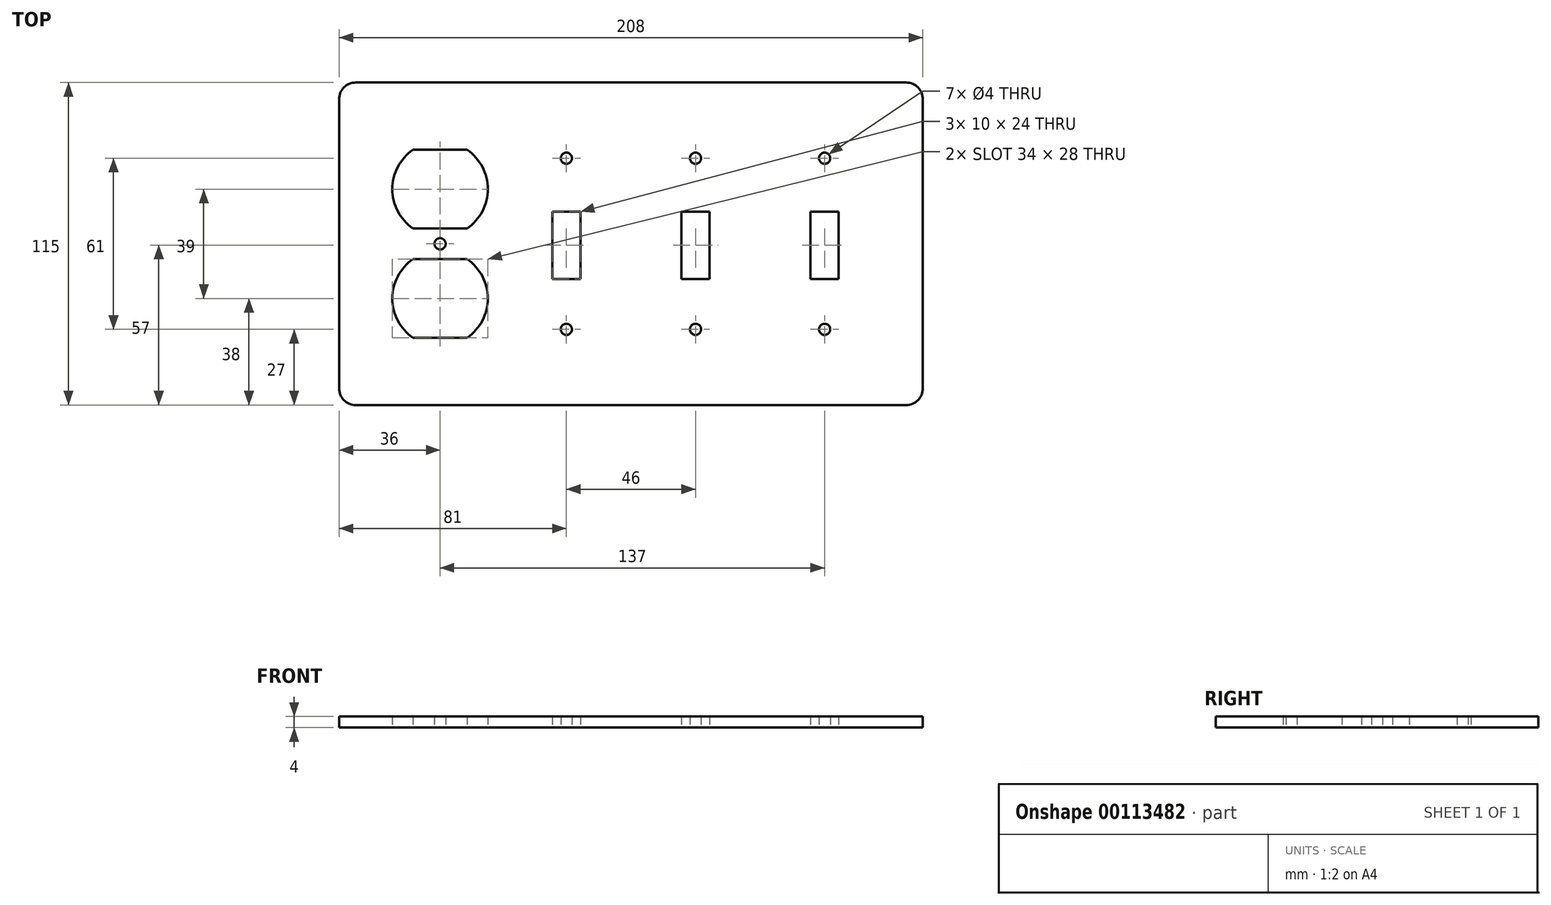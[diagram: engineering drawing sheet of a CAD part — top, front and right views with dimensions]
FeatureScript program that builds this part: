
annotation { "Feature Type Name" : "Feature", "Feature Type Description" : "" }
export const myFeature = defineFeature(function(context is Context, id is Id, definition is map)
    precondition{}
    {
        {
            var Q0;
            Q0=qCreatedBy(makeId("Top.planeOp"),FACE);
            var sketch = newSketch(context, id + "F0", { "sketchPlane" : qUnion([Q0])});
            skLineSegment(sketch, "E0.bottom", {"start": v(0, 0) * mm, "end": v(208, 0) * mm});
            skLineSegment(sketch, "E0.top", {"start": v(0, 115) * mm, "end": v(208, 115) * mm});
            skLineSegment(sketch, "E0.left", {"start": v(0, 0) * mm, "end": v(0, 115) * mm});
            skLineSegment(sketch, "E0.right", {"start": v(208, 0) * mm, "end": v(208, 115) * mm});
            skLineSegment(sketch, "E1.bottom", {"start": v(168, 69) * mm, "end": v(178, 69) * mm});
            skLineSegment(sketch, "E1.top", {"start": v(168, 45) * mm, "end": v(178, 45) * mm});
            skLineSegment(sketch, "E1.left", {"start": v(168, 69) * mm, "end": v(168, 45) * mm});
            skLineSegment(sketch, "E1.right", {"start": v(178, 69) * mm, "end": v(178, 45) * mm});
            skCircle(sketch, "E2", {"center": v(173, 88) * mm, "radius": 2 * mm});
            skCircle(sketch, "E3", {"center": v(173, 27) * mm, "radius": 2 * mm});
            skLineSegment(sketch, "E4.1.0.0", {"start": v(122, 69) * mm, "end": v(122, 45) * mm});
            skLineSegment(sketch, "E4.1.0.1", {"start": v(122, 45) * mm, "end": v(132, 45) * mm});
            skLineSegment(sketch, "E4.1.0.2", {"start": v(122, 69) * mm, "end": v(132, 69) * mm});
            skLineSegment(sketch, "E4.1.0.3", {"start": v(132, 69) * mm, "end": v(132, 45) * mm});
            skCircle(sketch, "E4.1.0.4", {"center": v(127, 88) * mm, "radius": 2 * mm});
            skCircle(sketch, "E4.1.0.5", {"center": v(127, 27) * mm, "radius": 2 * mm});
            skLineSegment(sketch, "E4.2.0.0", {"start": v(76, 69) * mm, "end": v(76, 45) * mm});
            skLineSegment(sketch, "E4.2.0.1", {"start": v(76, 45) * mm, "end": v(86, 45) * mm});
            skLineSegment(sketch, "E4.2.0.2", {"start": v(76, 69) * mm, "end": v(86, 69) * mm});
            skLineSegment(sketch, "E4.2.0.3", {"start": v(86, 69) * mm, "end": v(86, 45) * mm});
            skCircle(sketch, "E4.2.0.4", {"center": v(81, 88) * mm, "radius": 2 * mm});
            skCircle(sketch, "E4.2.0.5", {"center": v(81, 27) * mm, "radius": 2 * mm});
            skLineSegment(sketch, "E4.direction1", {"start": v(173, 27) * mm, "end": v(127, 27) * mm, "construction": true});
            skSolve(sketch);
        }
        {
            var Q0;
            Q0=qSketchRegion(id+"F0",true);
            extrude(context, id + "F1", {"entities" : qUnion([Q0]), "depth" : 4 * mm});
        }
        {
            var Q0;
            Q0=makeQuery(id+"F1.opExtrude","SWEPT_EDGE",EDGE,{"disambiguationData":[OSD([sQuery(id+"F0.wireOp",EDGE,"E0.top"),sQuery(id+"F0.wireOp",EDGE,"E0.left")])]});
            var Q1;
            Q1=makeQuery(id+"F1.opExtrude","SWEPT_EDGE",EDGE,{"disambiguationData":[OSD([sQuery(id+"F0.wireOp",EDGE,"E0.top"),sQuery(id+"F0.wireOp",EDGE,"E0.right")])]});
            var Q2;
            Q2=makeQuery(id+"F1.opExtrude","SWEPT_EDGE",EDGE,{"disambiguationData":[OSD([sQuery(id+"F0.wireOp",EDGE,"E0.bottom"),sQuery(id+"F0.wireOp",EDGE,"E0.right")])]});
            var Q3;
            Q3=makeQuery(id+"F1.opExtrude","SWEPT_EDGE",EDGE,{"disambiguationData":[OSD([sQuery(id+"F0.wireOp",EDGE,"E0.bottom"),sQuery(id+"F0.wireOp",EDGE,"E0.left")])]});
            fillet(context, id + "F2", {"entities" : qUnion([Q0, Q1, Q2, Q3]), "radius" : 6 * mm, "tangentPropagation" : true, "allowEdgeOverflow" : false});
        }
        {
            var Q0;
            Q0=makeQuery(id+"F1.opExtrude","CAP_FACE",FACE,{"disambiguationData":[OSD([sQuery(id+"F0.wireOp",EDGE,"E0.bottom"),sQuery(id+"F0.wireOp",EDGE,"E0.top"),sQuery(id+"F0.wireOp",EDGE,"E0.left"),sQuery(id+"F0.wireOp",EDGE,"E0.right"),sQuery(id+"F0.wireOp",EDGE,"E1.bottom"),sQuery(id+"F0.wireOp",EDGE,"E1.top"),sQuery(id+"F0.wireOp",EDGE,"E1.left"),sQuery(id+"F0.wireOp",EDGE,"E1.right"),sQuery(id+"F0.wireOp",EDGE,"E2"),sQuery(id+"F0.wireOp",EDGE,"E3")])],"isStart":false});
            var sketch = newSketch(context, id + "F3", { "sketchPlane" : qUnion([Q0])});
            skLineSegment(sketch, "E5.0.0", {"start": v(0, 109) * mm, "end": v(0, 6) * mm});
            skArc(sketch, "E5.0.1", {"start": v(0, 6) * mm, "mid": v(1.76, 1.76) * mm, "end": v(6, 0) * mm});
            skLineSegment(sketch, "E5.0.2", {"start": v(6, 0) * mm, "end": v(202, 0) * mm});
            skArc(sketch, "E5.0.3", {"start": v(202, 0) * mm, "mid": v(206.24, 1.76) * mm, "end": v(208, 6) * mm});
            skLineSegment(sketch, "E5.0.4", {"start": v(208, 6) * mm, "end": v(208, 109) * mm});
            skArc(sketch, "E5.0.5", {"start": v(208, 109) * mm, "mid": v(206.24, 113.24) * mm, "end": v(202, 115) * mm});
            skLineSegment(sketch, "E5.0.6", {"start": v(202, 115) * mm, "end": v(6, 115) * mm});
            skArc(sketch, "E5.0.7", {"start": v(6, 115) * mm, "mid": v(1.76, 113.24) * mm, "end": v(0, 109) * mm});
            skCircle(sketch, "E6.0", {"center": v(173, 88) * mm, "radius": 2 * mm});
            skLineSegment(sketch, "E7.0", {"start": v(168, 69) * mm, "end": v(178, 69) * mm});
            skLineSegment(sketch, "E8.0", {"start": v(178, 69) * mm, "end": v(178, 45) * mm});
            skLineSegment(sketch, "E9.0", {"start": v(168, 69) * mm, "end": v(168, 45) * mm});
            skLineSegment(sketch, "E10.0", {"start": v(168, 45) * mm, "end": v(178, 45) * mm});
            skCircle(sketch, "E11.0", {"center": v(173, 27) * mm, "radius": 2 * mm});
            skLineSegment(sketch, "E12", {"start": v(173, 69) * mm, "end": v(173, 45) * mm, "construction": true});
            skLineSegment(sketch, "E13", {"start": v(178, 57) * mm, "end": v(168, 57) * mm, "construction": true});
            skPoint(sketch, "E14", {"position": v(173, 57) * mm});
            skSolve(sketch);
        }
        {
            var Q0;
            Q0=qCreatedBy(makeId("Top.planeOp"),FACE);
            var sketch = newSketch(context, id + "F4", { "sketchPlane" : qUnion([Q0])});
            skCircle(sketch, "E15", {"center": v(36, 57.5) * mm, "radius": 2 * mm});
            skCircle(sketch, "E16", {"center": v(36, 77) * mm, "radius": 17 * mm});
            skCircle(sketch, "E17", {"center": v(36, 38) * mm, "radius": 17 * mm});
            skSolve(sketch);
        }
        {
            var Q0;
            Q0 = qSketchRegion(id + "F4", true);
            extrude(context, id + "F5", {"entities" : qUnion([Q0]), "operationType" : NewBodyOperationType.REMOVE, "depth" : 25 * mm, "offsetDistance" : 25 * mm});
        }
        {
            var Q0;
            Q0=makeQuery(id+"F3.imprint","IMPRINT",FACE,{"disambiguationData":[TD([[makeQuery(id+"F3.imprint","IMPRINT",EDGE,{"derivedFrom":sQuery(id+"F3.wireOp",EDGE,"E5.0.0")}),-1.0]])]});
            var sketch = newSketch(context, id + "F6", { "sketchPlane" : qUnion([Q0])});
            skLineSegment(sketch, "E18", {"start": v(25.33, 91) * mm, "end": v(46.06, 91) * mm});
            skLineSegment(sketch, "E19", {"start": v(46.06, 91) * mm, "end": v(43.26, 94.42) * mm});
            skLineSegment(sketch, "E20", {"start": v(43.26, 94.42) * mm, "end": v(32.74, 94.84) * mm});
            skLineSegment(sketch, "E21", {"start": v(32.74, 94.84) * mm, "end": v(25.33, 91) * mm});
            skLineSegment(sketch, "E22.bottom", {"start": v(51.19, 59.8) * mm, "end": v(23.64, 59.8) * mm});
            skLineSegment(sketch, "E22.top", {"start": v(51.19, 63) * mm, "end": v(23.64, 63) * mm});
            skLineSegment(sketch, "E22.left", {"start": v(51.19, 59.8) * mm, "end": v(51.19, 63) * mm});
            skLineSegment(sketch, "E22.right", {"start": v(23.64, 59.8) * mm, "end": v(23.64, 63) * mm});
            skLineSegment(sketch, "E23.bottom", {"start": v(22.68, 55.04) * mm, "end": v(51.71, 55.04) * mm});
            skLineSegment(sketch, "E23.top", {"start": v(22.68, 52) * mm, "end": v(51.71, 52) * mm});
            skLineSegment(sketch, "E23.left", {"start": v(22.68, 55.04) * mm, "end": v(22.68, 52) * mm});
            skLineSegment(sketch, "E23.right", {"start": v(51.71, 55.04) * mm, "end": v(51.71, 52) * mm});
            skLineSegment(sketch, "E24.bottom", {"start": v(20.13, 24) * mm, "end": v(53.35, 24) * mm});
            skLineSegment(sketch, "E24.top", {"start": v(20.13, 21) * mm, "end": v(53.35, 21) * mm});
            skLineSegment(sketch, "E24.left", {"start": v(20.13, 24) * mm, "end": v(20.13, 21) * mm});
            skLineSegment(sketch, "E24.right", {"start": v(53.35, 24) * mm, "end": v(53.35, 21) * mm});
            skSolve(sketch);
        }
        {
            var Q0;
            Q0 = qSketchRegion(id + "F6", true);
            extrude(context, id + "F7", {"entities" : qUnion([Q0]), "operationType" : NewBodyOperationType.ADD, "oppositeDirection" : true, "depth" : 4 * mm, "offsetDistance" : 25 * mm});
        }
    });
